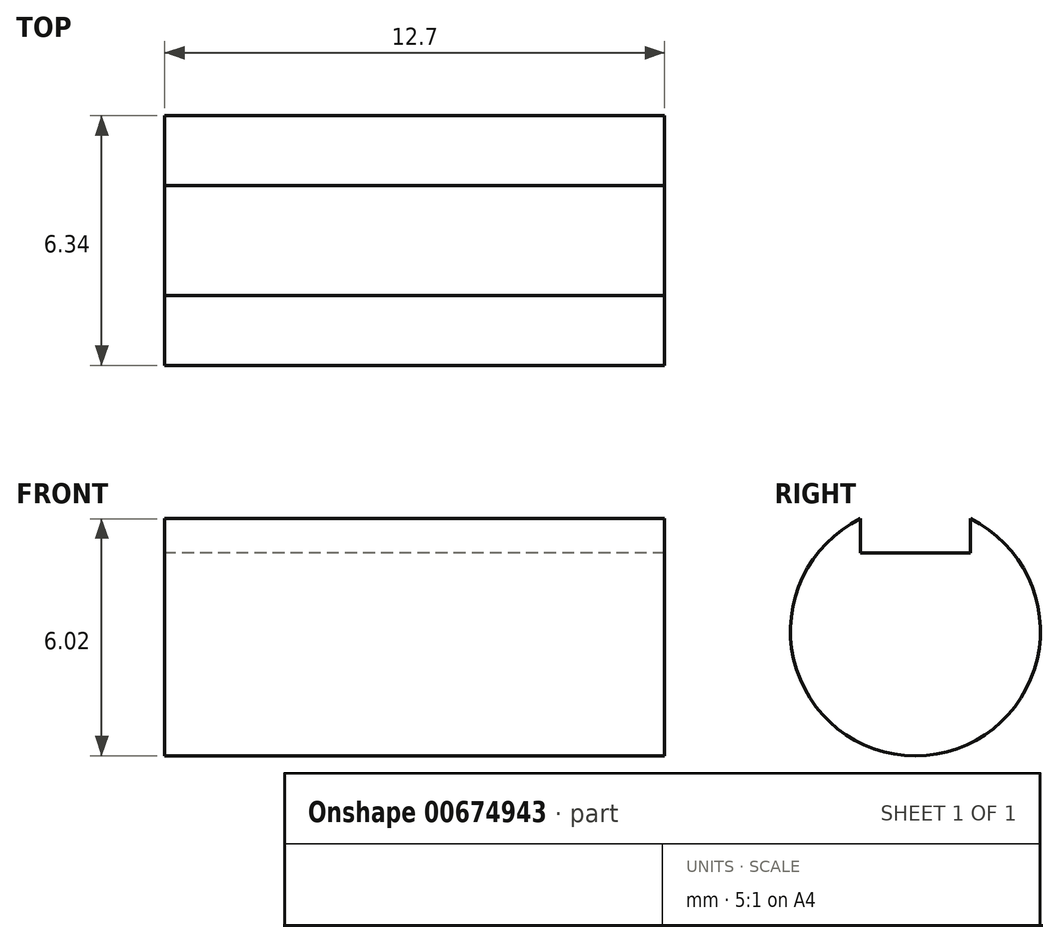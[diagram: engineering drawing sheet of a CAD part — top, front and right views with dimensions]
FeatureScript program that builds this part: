
annotation { "Feature Type Name" : "Feature", "Feature Type Description" : "" }
export const myFeature = defineFeature(function(context is Context, id is Id, definition is map)
    precondition{}
    {
        {
            var Q0;
            Q0=qCreatedBy(makeId("Front.planeOp"),FACE);
            var sketch = newSketch(context, id + "F0", { "sketchPlane" : qUnion([Q0])});
            skLineSegment(sketch, "E0.bottom", {"start": v(0, 0) * mm, "end": v(-11.94, 0) * mm});
            skLineSegment(sketch, "E0.left", {"start": v(0, 0) * mm, "end": v(0, 26.47) * mm});
            skLineSegment(sketch, "E0.right", {"start": v(-11.94, 0) * mm, "end": v(-11.94, 15.88) * mm});
            skPoint(sketch, "E1", {"position": v(-11.94, 15.88) * mm});
            skEllipticalArc(sketch, "E2", {});
            skPoint(sketch, "E3.orphan", {"position": v(-11.94, 31.75) * mm});
            skPoint(sketch, "E4.visualSharp", {"position": v(0, 31.75) * mm});
            skArc(sketch, "E4.filletArc", {"start": v(0, 26.47) * mm, "mid": v(-2.17, 29.91) * mm, "end": v(-6.2, 29.44) * mm});
            const initialGuessF0  = {"E2": [0, 0.015875, -1, 0, 0.011938, 0.015875, 5.259172195956843, 6.283185307179586]};
            skSetInitialGuess(sketch, initialGuessF0);
            skSolve(sketch);
        }
        {
            var Q0;
            Q0=makeQuery(id+"F0.imprint","IMPRINT",FACE,{"disambiguationData":[TD([[makeQuery(id+"F0.imprint","IMPRINT",EDGE,{"derivedFrom":sQuery(id+"F0.wireOp",EDGE,"E0.bottom")}),-1.0]])]});
            var Q1;
            Q1=sQuery(id+"F0.wireOp",EDGE,"E0.bottom");
            revolve(context, id + "F1", {"entities" : qUnion([Q0]), "axis" : qUnion([Q1]), "revolveType" : RevolveType.FULL});
        }
        {
            var Q0;
            Q0=makeQuery(id+"F1.opRevolve","SWEPT_FACE",FACE,{"disambiguationData":[OSD([sQuery(id+"F0.wireOp",EDGE,"E0.left")])]});
            var sketch = newSketch(context, id + "F2", { "sketchPlane" : qUnion([Q0])});
            skCircle(sketch, "E5.0.0", {"center": v(0, 0) * mm, "radius": 26.47 * mm});
            skSolve(sketch);
        }
        {
            var Q0;
            Q0=sQuery(id+"F2.wireOp",VERTEX,"E5.0.0.center");
            var Q1;
            Q1=makeQuery(id+"F1.opRevolve","SWEPT_BODY",BODY,{"disambiguationData":[OSD([sQuery(id+"F0.wireOp",EDGE,"E0.bottom"),sQuery(id+"F0.wireOp",EDGE,"E0.left"),sQuery(id+"F0.wireOp",EDGE,"E0.right"),sQuery(id+"F0.wireOp",EDGE,"E2"),sQuery(id+"F0.wireOp",EDGE,"E4.filletArc")])]});
            hole(context, id + "F3", {"style" : HoleStyle.SIMPLE, "endStyle" : HoleEndStyle.BLIND, "standardTappedOrClearance" : lookupTablePath({ "standard" : "ANSI", "fit" : "Normal (ASME)", "size" : "1/4", "type" : "Clearance" }), "standardBlindInLast" : lookupTablePath({ "fit" : "Free", "standard" : "ANSI", "size" : "1/4", "type" : "Clearance" }), "holeDiameter" : 6.76 * mm, "majorDiameter" : 6.35 * mm, "holeDepth" : 5.08 * mm, "isTappedThrough" : true, "tappedDepth" : 13.5 * mm, "tapClearance" : 3, "startFromSketch" : true, "locations" : qUnion([Q0]), "scope" : qUnion([Q1])});
        }
        {
            var Q0;
            Q0=makeQuery(id+"F1.opRevolve","SWEPT_FACE",FACE,{"disambiguationData":[OSD([sQuery(id+"F0.wireOp",EDGE,"E0.left")])]});
            var sketch = newSketch(context, id + "F4", { "sketchPlane" : qUnion([Q0])});
            skLineSegment(sketch, "E6.bottom", {"start": v(1.2, 2.19) * mm, "end": v(-1.2, 2.19) * mm});
            skLineSegment(sketch, "E6.top", {"start": v(1.2, 4.57) * mm, "end": v(-1.2, 4.57) * mm});
            skLineSegment(sketch, "E6.left", {"start": v(1.2, 2.19) * mm, "end": v(1.2, 4.57) * mm});
            skLineSegment(sketch, "E6.right", {"start": v(-1.2, 2.19) * mm, "end": v(-1.2, 4.57) * mm});
            skPoint(sketch, "E6.middle", {"position": v(0, 3.38) * mm});
            skSolve(sketch);
        }
        {
            var Q0;
            {var subQ0=sQuery(id+"F4.wireOp",EDGE,"E6.bottom");Q0=makeQuery(id+"F4.imprint","IMPRINT",FACE,{"disambiguationData":[TD([[makeQuery(id+"F4.imprint","IMPRINT",EDGE,{"derivedFrom":subQ0}),-1.0]])]});}
            extrude(context, id + "F5", {"entities" : qUnion([Q0]), "operationType" : NewBodyOperationType.ADD, "endBound" : BoundingType.UP_TO_NEXT, "oppositeDirection" : true, "depth" : 25.4 * mm, "offsetDistance" : 25.4 * mm});
        }
        {
            var Q0;
            Q0=makeQuery(id+"F1.opRevolve","SWEPT_FACE",FACE,{"disambiguationData":[OSD([sQuery(id+"F0.wireOp",EDGE,"E0.right")])]});
            var sketch = newSketch(context, id + "F6", { "sketchPlane" : qUnion([Q0])});
            skText(sketch, "E7", { "text": "H", "fontName": "OpenSans-Bold.ttf"});
            const initialGuessF6  = {"E7": [-0.01138, -0.01107, 1, 0, 0.02215]};
            skSetInitialGuess(sketch, initialGuessF6);
            skSolve(sketch);
        }
        {
            var Q0;
            Q0=makeQuery(id+"F6.imprint","IMPRINT",FACE,{"disambiguationData":[TD([[makeQuery(id+"F6.imprint","IMPRINT",EDGE,{"derivedFrom":sQuery(id+"F6.wireOp",EDGE,"E7.sketch_text.stroke-0")}),-1.0]])]});
            extrude(context, id + "F7", {"entities" : qUnion([Q0]), "operationType" : NewBodyOperationType.REMOVE, "oppositeDirection" : true, "depth" : 1.27 * mm, "offsetDistance" : 25.4 * mm});
        }
        {
            var Q0;
            Q0=makeQuery(id+"F5.boolean.opBoolean","MERGE",FACE,{"derivedFrom":[makeQuery(id+"F1.opRevolve","SWEPT_FACE",FACE,{"disambiguationData":[OSD([sQuery(id+"F0.wireOp",EDGE,"E0.left")])]}),makeQuery(id+"F5.opExtrude","CAP_FACE",FACE,{"disambiguationData":[OSD([sQuery(id+"F3.hole-0.sketch.wireOp",EDGE,"core_line_2"),sQuery(id+"F3.hole-0.sketch.wireOp",EDGE,"core_line_3"),sQuery(id+"F4.wireOp",EDGE,"E6.bottom"),sQuery(id+"F4.wireOp",EDGE,"E6.left"),sQuery(id+"F4.wireOp",EDGE,"E6.right")])],"isStart":true})]});
            var sketch = newSketch(context, id + "F8", { "sketchPlane" : qUnion([Q0])});
            skArc(sketch, "E8.0", {"start": v(-1.2, 3.16) * mm, "mid": v(0, -3.38) * mm, "end": v(1.2, 3.16) * mm});
            skLineSegment(sketch, "E9.0", {"start": v(1.2, 2.19) * mm, "end": v(-1.2, 2.19) * mm});
            skLineSegment(sketch, "E10.0", {"start": v(1.2, 2.19) * mm, "end": v(1.2, 3.16) * mm});
            skLineSegment(sketch, "E11.0", {"start": v(-1.2, 2.19) * mm, "end": v(-1.2, 3.16) * mm});
            skArc(sketch, "E12.0", {"start": v(-1.4, 2.85) * mm, "mid": v(0, -3.18) * mm, "end": v(1.4, 2.85) * mm});
            skLineSegment(sketch, "E12.1", {"start": v(-1.4, 1.98) * mm, "end": v(-1.4, 2.85) * mm});
            skLineSegment(sketch, "E12.2", {"start": v(1.4, 1.98) * mm, "end": v(-1.4, 1.98) * mm});
            skLineSegment(sketch, "E12.3", {"start": v(1.4, 1.98) * mm, "end": v(1.4, 2.85) * mm});
            skSolve(sketch);
        }
        {
            var Q0;
            Q0=makeQuery(id+"F8.imprint","IMPRINT",FACE,{"disambiguationData":[TD([[makeQuery(id+"F8.imprint","IMPRINT",EDGE,{"derivedFrom":sQuery(id+"F8.wireOp",EDGE,"E12.0")}),1.0]])]});
            extrude(context, id + "F9", {"entities" : qUnion([Q0]), "depth" : 12.7 * mm, "offsetDistance" : 25.4 * mm});
        }
        {
            var Q0;
            Q0=makeQuery(id+"F1.opRevolve","SWEPT_BODY",BODY,{"disambiguationData":[OSD([sQuery(id+"F0.wireOp",EDGE,"E0.bottom"),sQuery(id+"F0.wireOp",EDGE,"E0.left"),sQuery(id+"F0.wireOp",EDGE,"E0.right"),sQuery(id+"F0.wireOp",EDGE,"E2"),sQuery(id+"F0.wireOp",EDGE,"E4.filletArc")])]});
            deleteBodies(context, id + "F10", {"entities" : qUnion([Q0])});
        }
    });
